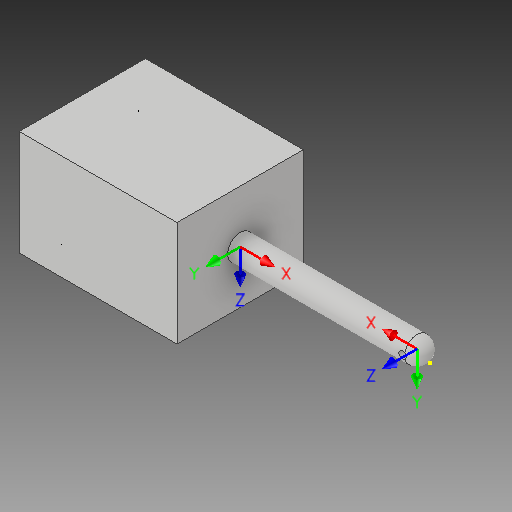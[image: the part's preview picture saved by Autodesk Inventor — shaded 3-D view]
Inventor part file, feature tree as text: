
AUTODESK INVENTOR PART (.ipt)
format: ipt  version: 2019 (Build 230136000, 136)  size: 137,728 bytes
history: native  units: in
note: dims shown in document units (in); Inventor stores cm internally (conversion verified against a paired STEP export)
features: other x18, sketch x5, extrude x2, revolve x1, fillet x1
ambient origin geometry x8: Origin, YZ Plane, XZ Plane, XY Plane, X Axis, Y Axis, Z Axis, Center Point
bodies: Solid1 (feature_tree)
feature tree (27):
  other  "Annotations"
  revolve  "Revolution1"  [1 undecoded]
  sketch  "Sketch2"  dims[d3=0.4724in]
  fillet  "Fillet1"  [1 undecoded]
  sketch  "Sketch3"  dims[d4=0.0in d5=0.0in d6=0.0in d7=0.0in d8=0.0in d9=0.0in d10=0.2756in]
  other  "UCS1"
  extrude  "Extrusion1"  Depth=0.2756in
  other  "UCS2"
  extrude  "Extrusion2"  Depth=4.7244in
  sketch  "Sketch1"  dims[d0=7.0866in d1=0.4724in d2=90.0deg]
  sketch  "Sketch4"  dims[d11=3.1496in d12=0.0in]
  sketch  "Sketch5"  dims[d13=0.0in d14=0.0in d15=0.0in d16=0.0in d17=0.0in d18=0.0in d19=4.7244in d20=5.9055in d21=2.3622in d22=3.937in d23=0.0in d24=0.29in d25=0.0227in d26=90.0deg]
  other  "UCS1: YZ Plane"
  other  "UCS1: XZ Plane"
  other  "UCS1: XY Plane"
  other  "UCS1: X Axis"
  other  "UCS1: Y Axis"
  other  "UCS1: Z Axis"
  other  "UCS1: Center Point"
  other  "UCS2: YZ Plane"
  other  "UCS2: XZ Plane"
  other  "UCS2: XY Plane"
  other  "UCS2: X Axis"
  other  "UCS2: Y Axis"
  other  "UCS2: Z Axis"
  other  "UCS2: Center Point"
  other  "Angular Dimension 1"
note: 2 required parameter values undecoded (feature->parameter linkage not recoverable at this tier; creation-order binding heuristic only, values carry confidence <= 0.55)